# Revit family: Skylight-Wasco-DDSA2-Pyramid
name_source: partatom
category: Windows
revit_build: Autodesk Revit 2015 (Build: 20140606_1530(x64)
units: mm (PartAtom-declared; Revit-internal decimal feet)

## types (19) — shared parameters
12in Curb Height = No
16in Curb Height = Yes
4CH = No
A = 13.37°
Acrylic Glazing Inner = Acrylic - Wasco - Clear
Acrylic Glazing Outer = Acrylic - Wasco - Clear
Curb Height = 1' - 4"
Curb Width = 0' - 1 1/2"
Default Elevation = 0' - 0"
Description = Skylight
Finish = Aluminum - Wasco - Mill
Frame = Plastic - Wasco - Vinyl
Host Constraint = 1
Inner Curb = Metal - Wasco - White
Manufacturer = Wasco
Outer Curb = Aluminum - Wasco - Mill
Overhang = 0' - 1 25/32"
Product Documentation Link = http://www.wascoskylights.com
Product Name = SSP Pyramid Fall Protection
Product Page URL = http://www.wascoskylights.com
Type Comments = Maximum length and width = 95.5in x 95.5in.  Long leg to short leg maximum ratio cannot be more than 2.3.
URL = http://www.wascoskylights.com

## per-type parameters (varying)
| type | Altitude | Height | Host Length | Host Width | L | Length | Rough Height | Rough Length | Rough Width | Width |
| DDSA2828 | 0' - 2 25/32" | 0' - 2 25/32" | 4' - 1 1/4" | 4' - 1 1/4" | 0' - 11 11/16" | 2' - 1 1/4" | 1' - 7 5/16" | 2' - 3 1/32" | 2' - 3 1/32" | 2' - 1 1/4" |
| DDSA2852 | 0' - 2 25/32" | 0' - 2 25/32" | 6' - 1 1/4" | 4' - 1 1/4" | 0' - 11 11/16" | 4' - 1 1/4" | 1' - 7 5/16" | 4' - 3 1/32" | 2' - 3 1/32" | 2' - 1 1/4" |
| DDSA3636 | 0' - 3 23/32" | 0' - 3 23/32" | 4' - 9 1/4" | 4' - 9 1/4" | 1' - 3 11/16" | 2' - 9 1/4" | 1' - 8 1/4" | 2' - 11 1/32" | 2' - 11 1/32" | 2' - 9 1/4" |
| DDSA3652 | 0' - 3 23/32" | 0' - 3 23/32" | 6' - 0 1/4" | 4' - 9 1/4" | 1' - 3 11/16" | 4' - 0 1/4" | 1' - 8 1/4" | 4' - 2 1/32" | 2' - 11 1/32" | 2' - 9 1/4" |
| DDSA4242 | 0' - 4 17/32" | 0' - 4 17/32" | 5' - 4" | 5' - 4" | 1' - 7 1/16" | 3' - 4" | 1' - 9 1/16" | 3' - 5 25/32" | 3' - 5 25/32" | 3' - 4" |
| DDSA5252 | 0' - 5 5/8" | 0' - 5 5/8" | 6' - 1 1/4" | 6' - 1 1/4" | 1' - 11 11/16" | 4' - 1 1/4" | 1' - 10 5/32" | 4' - 3 1/32" | 4' - 3 1/32" | 4' - 1 1/4" |
| DDSA5276 | 0' - 5 5/8" | 0' - 5 5/8" | 8' - 0 1/2" | 6' - 1 1/4" | 1' - 11 11/16" | 6' - 0 1/2" | 1' - 10 5/32" | 6' - 2 9/32" | 4' - 3 1/32" | 4' - 1 1/4" |
| DDSA5296 | 0' - 5 5/8" | 0' - 5 5/8" | 9' - 8 1/2" | 6' - 1 1/4" | 1' - 11 11/16" | 7' - 8 1/2" | 1' - 10 5/32" | 7' - 10 9/32" | 4' - 3 1/32" | 4' - 1 1/4" |
| DDSA5555 | 0' - 5 27/32" | 0' - 5 27/32" | 6' - 3" | 6' - 3" | 2' - 0 9/16" | 4' - 3" | 1' - 10 3/8" | 4' - 4 25/32" | 4' - 4 25/32" | 4' - 3" |
| DDSA55102 | 0' - 5 27/32" | 0' - 5 27/32" | 10' - 3" | 6' - 3" | 2' - 0 9/16" | 8' - 3" | 1' - 10 3/8" | 8' - 4 25/32" | 4' - 4 25/32" | 4' - 3" |
| DDSA6060 | 0' - 6 21/32" | 0' - 6 21/32" | 6' - 10" | 6' - 10" | 2' - 4 1/16" | 4' - 10" | 1' - 11 3/16" | 4' - 11 25/32" | 4' - 11 25/32" | 4' - 10" |
| DDSA6666 | 0' - 7 1/4" | 0' - 7 1/4" | 7' - 3" | 7' - 3" | 2' - 6 9/16" | 5' - 3" | 1' - 11 25/32" | 5' - 4 25/32" | 5' - 4 25/32" | 5' - 3" |
| DDSA66102 | 0' - 7 1/4" | 0' - 7 1/4" | 10' - 3" | 7' - 3" | 2' - 6 9/16" | 8' - 3" | 1' - 11 25/32" | 8' - 4 25/32" | 5' - 4 25/32" | 5' - 3" |
| DDSA6476 | 0' - 6 31/32" | 0' - 6 31/32" | 8' - 0 1/2" | 7' - 0 1/2" | 2' - 5 5/16" | 6' - 0 1/2" | 1' - 11 1/2" | 6' - 2 9/32" | 5' - 2 9/32" | 5' - 0 1/2" |
| DDSA6496 | 0' - 6 31/32" | 0' - 6 31/32" | 9' - 8 1/2" | 7' - 0 1/2" | 2' - 5 5/16" | 7' - 8 1/2" | 1' - 11 1/2" | 7' - 10 9/32" | 5' - 2 9/32" | 5' - 0 1/2" |
| DDSA7272 | 0' - 8 7/32" | 0' - 8 7/32" | 7' - 11" | 7' - 11" | 2' - 10 9/16" | 5' - 11" | 2' - 0 3/4" | 6' - 0 25/32" | 6' - 0 25/32" | 5' - 11" |
| DDSA8080 | 0' - 9 1/32" | 0' - 9 1/32" | 8' - 6" | 8' - 6" | 3' - 2 1/16" | 6' - 6" | 2' - 1 9/16" | 6' - 7 25/32" | 6' - 7 25/32" | 6' - 6" |
| DDSA9898 | 0' - 11 1/8" | 0' - 11 1/8" | 9' - 11 1/2" | 9' - 11 1/2" | 3' - 10 13/16" | 7' - 11 1/2" | 2' - 3 21/32" | 8' - 1 9/32" | 8' - 1 9/32" | 7' - 11 1/2" |
| Custom | 0' - 5 15/32" | 0' - 5 15/32" | 6' - 0" | 6' - 0" | 1' - 11 1/16" | 4' - 0" | 1' - 10" | 4' - 1 25/32" | 4' - 1 25/32" | 4' - 0" |

note: column(s) folded — value = type name in every type: Model

## geometry (parser evidence)
native form markers: Blend x1, Sweep x3
no freeform markers — native parametric forms only
